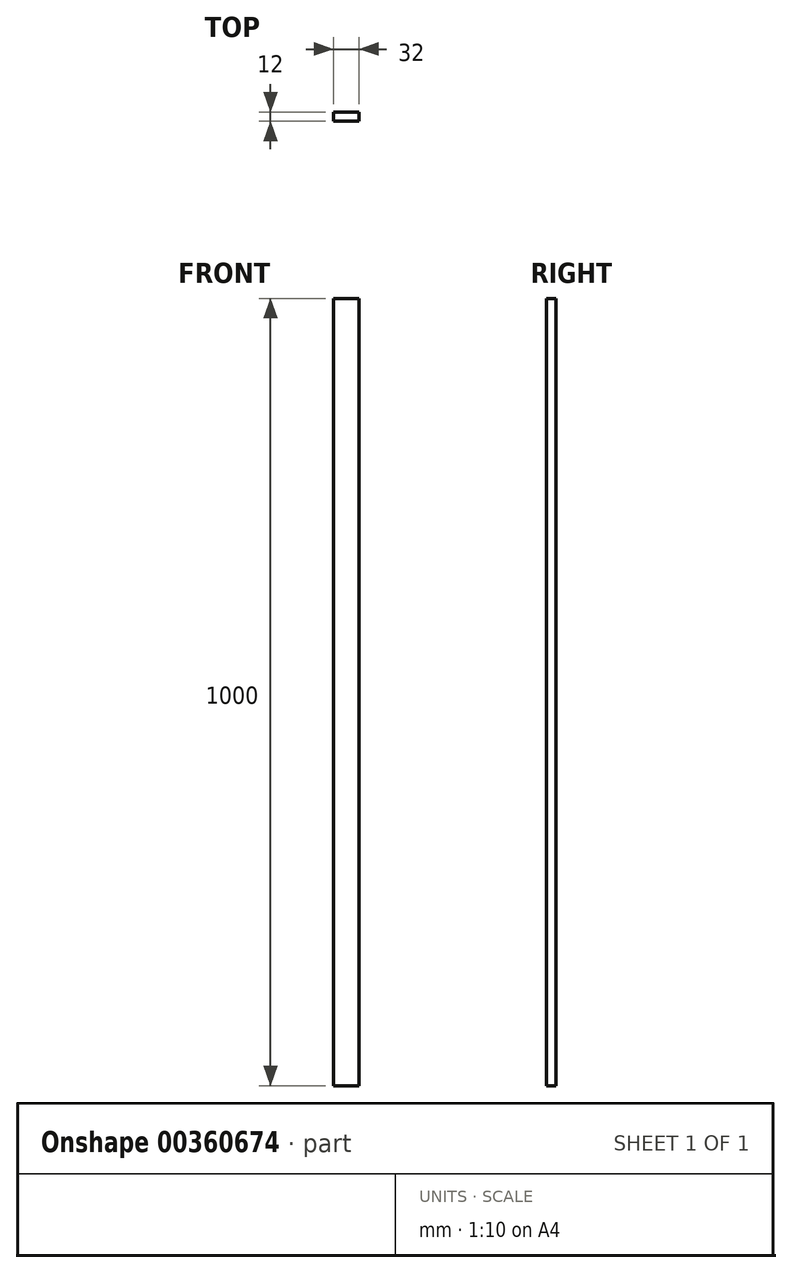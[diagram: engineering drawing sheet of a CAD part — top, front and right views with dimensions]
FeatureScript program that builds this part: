
annotation { "Feature Type Name" : "Feature", "Feature Type Description" : "" }
export const myFeature = defineFeature(function(context is Context, id is Id, definition is map)
    precondition{}
    {
        {
            var Q0;
            Q0=qCreatedBy(makeId("Front.planeOp"),FACE);
            var sketch = newSketch(context, id + "F0", { "sketchPlane" : qUnion([Q0])});
            skLineSegment(sketch, "E0.bottom", {"start": v(0, 0) * mm, "end": v(32, 0) * mm});
            skLineSegment(sketch, "E0.top", {"start": v(0, 1000) * mm, "end": v(32, 1000) * mm});
            skLineSegment(sketch, "E0.left", {"start": v(0, 0) * mm, "end": v(0, 1000) * mm});
            skLineSegment(sketch, "E0.right", {"start": v(32, 0) * mm, "end": v(32, 1000) * mm});
            skSolve(sketch);
        }
        {
            var Q0;
            Q0=makeQuery(id+"F0.imprint","IMPRINT",FACE,{"disambiguationData":[TD([[makeQuery(id+"F0.imprint","IMPRINT",EDGE,{"derivedFrom":sQuery(id+"F0.wireOp",EDGE,"E0.bottom")}),1.0]])]});
            extrude(context, id + "F1", {"entities" : qUnion([Q0]), "depth" : 12 * mm});
        }
    });
